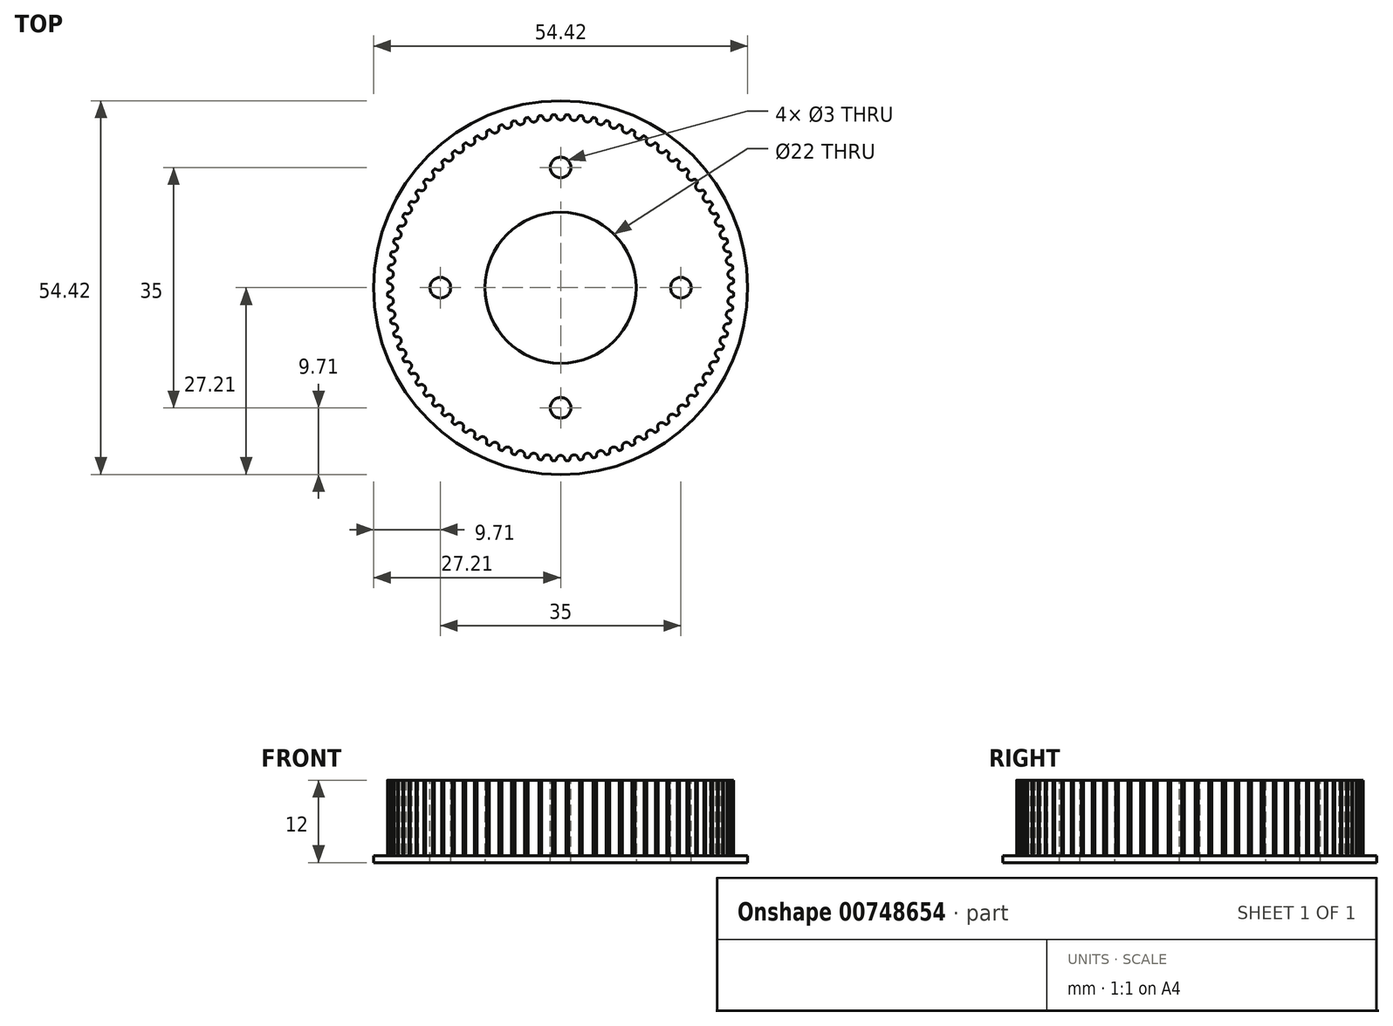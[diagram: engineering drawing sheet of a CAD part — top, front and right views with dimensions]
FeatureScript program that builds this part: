
annotation { "Feature Type Name" : "Feature", "Feature Type Description" : "" }
export const myFeature = defineFeature(function(context is Context, id is Id, definition is map)
    precondition{}
    {
        {
            assignVariable(context, id + "F0", {"name" : "Teeth", "anyValue" : 80});
        }
        {
            var Q0;
            Q0=qCreatedBy(makeId("Top.planeOp"),FACE);
            var sketch = newSketch(context, id + "F1", { "sketchPlane" : qUnion([Q0])});
            skCircle(sketch, "E0", {"center": v(0, 0) * mm, "radius": 25.21 * mm});
            skSolve(sketch);
        }
        {
            var Q0;
            Q0=qCreatedBy(makeId("Top.planeOp"),FACE);
            var sketch = newSketch(context, id + "F2", { "sketchPlane" : qUnion([Q0])});
            skArc(sketch, "E1.0", {"start": v(0.79, 25.2) * mm, "mid": v(0, 25.21) * mm, "end": v(-0.79, 25.2) * mm});
            skLineSegment(sketch, "E2", {"start": v(0, 0) * mm, "end": v(0, 25.03) * mm, "construction": true});
            skArc(sketch, "E3", {"start": v(0, 24.42) * mm, "mid": v(-0.38, 24.56) * mm, "end": v(-0.6, 24.9) * mm});
            skArc(sketch, "E4", {"start": v(-0.6, 24.9) * mm, "mid": v(-0.63, 25) * mm, "end": v(-0.68, 25.1) * mm});
            skArc(sketch, "E5", {"start": v(-0.68, 25.1) * mm, "mid": v(-0.72, 25.16) * mm, "end": v(-0.79, 25.2) * mm});
            skArc(sketch, "E6.MirrorCS", {"start": v(0, 24.42) * mm, "mid": v(0.38, 24.56) * mm, "end": v(0.6, 24.9) * mm});
            skArc(sketch, "E7.MirrorCS", {"start": v(0.68, 25.1) * mm, "mid": v(0.72, 25.16) * mm, "end": v(0.79, 25.2) * mm});
            skArc(sketch, "E8.MirrorCS", {"start": v(0.6, 24.9) * mm, "mid": v(0.63, 25) * mm, "end": v(0.68, 25.1) * mm});
            skSolve(sketch);
        }
        {
            var Q0;
            Q0=qSketchRegion(id+"F1",true);
            extrude(context, id + "F3", {"entities" : qUnion([Q0]), "depth" : 11 * mm, "offsetDistance" : 25 * mm});
        }
        {
            var Q0;
            Q0=makeQuery(id+"F2.imprint","IMPRINT",FACE,{"disambiguationData":[TD([[makeQuery(id+"F2.imprint","IMPRINT",EDGE,{"derivedFrom":sQuery(id+"F2.wireOp",EDGE,"E1.0")}),1.0]])]});
            extrude(context, id + "F4", {"entities" : qUnion([Q0]), "depth" : 25 * mm, "offsetDistance" : 25 * mm});
        }
        {
            var Q0;
            Q0=makeQuery(id+"F4.opExtrude","SWEPT_BODY",BODY,{"disambiguationData":[OSD([sQuery(id+"F2.wireOp",EDGE,"E1.0"),sQuery(id+"F2.wireOp",EDGE,"E3"),sQuery(id+"F2.wireOp",EDGE,"E4"),sQuery(id+"F2.wireOp",EDGE,"E5"),sQuery(id+"F2.wireOp",EDGE,"E6.MirrorCS"),sQuery(id+"F2.wireOp",EDGE,"E7.MirrorCS"),sQuery(id+"F2.wireOp",EDGE,"E8.MirrorCS")])]});
            var Q1;
            Q1=sQuery(id+"F1.wireOp",EDGE,"E0");
            circularPattern(context, id + "F5", {"operationType" : NewBodyOperationType.REMOVE, "entities" : qUnion([Q0]), "axis" : qUnion([Q1]), "angle" : 360 * degree, "instanceCount" : getVariable(context, 'Teeth'), "equalSpace" : true});
        }
        {
            var Q0;
            Q0=qCreatedBy(makeId("Top.planeOp"),FACE);
            var sketch = newSketch(context, id + "F6", { "sketchPlane" : qUnion([Q0])});
            skCircle(sketch, "E9", {"center": v(0, 0) * mm, "radius": 11 * mm});
            skSolve(sketch);
        }
        {
            var Q0;
            Q0=qSketchRegion(id+"F6",true);
            var Q1;
            Q1=sQuery(id+"F6.wireOp",EDGE,"E9");
            extrude(context, id + "F7", {"entities" : qUnion([Q0]), "operationType" : NewBodyOperationType.REMOVE, "surfaceEntities" : qUnion([Q1]), "endBound" : BoundingType.THROUGH_ALL, "depth" : 25 * mm, "offsetDistance" : 25 * mm});
        }
        {
            var Q0;
            Q0=qCreatedBy(makeId("Top.planeOp"),FACE);
            var sketch = newSketch(context, id + "F8", { "sketchPlane" : qUnion([Q0])});
            skCircle(sketch, "E10", {"center": v(0, 0) * mm, "radius": 26.21 * mm});
            skCircle(sketch, "E11.0", {"center": v(0, 0) * mm, "radius": 11 * mm});
            skCircle(sketch, "E12.0", {"center": v(0, 0) * mm, "radius": 27.21 * mm});
            skSolve(sketch);
        }
        {
            var Q0;
            Q0=makeQuery(id+"F3.opExtrude","CAP_FACE",FACE,{"disambiguationData":[OSD([sQuery(id+"F1.wireOp",EDGE,"E0")])],"isStart":false});
            var sketch = newSketch(context, id + "F9", { "sketchPlane" : qUnion([Q0])});
            skLineSegment(sketch, "E13", {"start": v(0, 0) * mm, "end": v(0, 17.5) * mm, "construction": true});
            skLineSegment(sketch, "E14", {"start": v(0, 0) * mm, "end": v(17.5, 0) * mm, "construction": true});
            skLineSegment(sketch, "E15", {"start": v(0, 0) * mm, "end": v(0, -17.5) * mm, "construction": true});
            skLineSegment(sketch, "E16", {"start": v(0, 0) * mm, "end": v(-17.5, 0) * mm, "construction": true});
            skCircle(sketch, "E17", {"center": v(0, 17.5) * mm, "radius": 1.5 * mm});
            skCircle(sketch, "E18", {"center": v(-17.5, 0) * mm, "radius": 1.5 * mm});
            skCircle(sketch, "E19", {"center": v(17.5, 0) * mm, "radius": 1.5 * mm});
            skCircle(sketch, "E20", {"center": v(0, -17.5) * mm, "radius": 1.5 * mm});
            skSolve(sketch);
        }
        {
            var Q0;
            Q0=makeQuery(id+"F8.imprint","IMPRINT",FACE,{"disambiguationData":[TD([[makeQuery(id+"F8.imprint","IMPRINT",EDGE,{"derivedFrom":sQuery(id+"F8.wireOp",EDGE,"E10")}),-1.0]])]});
            var Q1;
            Q1=makeQuery(id+"F8.imprint","IMPRINT",FACE,{"disambiguationData":[TD([[makeQuery(id+"F8.imprint","IMPRINT",EDGE,{"derivedFrom":sQuery(id+"F8.wireOp",EDGE,"E10")}),1.0]])]});
            var Q2;
            Q2=makeQuery(id+"F8.imprint","IMPRINT",FACE,{"disambiguationData":[TD([[makeQuery(id+"F8.imprint","IMPRINT",EDGE,{"derivedFrom":sQuery(id+"F8.wireOp",EDGE,"E11.0")}),1.0]])]});
            extrude(context, id + "F10", {"entities" : qUnion([Q0, Q1, Q2]), "operationType" : NewBodyOperationType.ADD, "oppositeDirection" : true, "depth" : 1 * mm, "offsetDistance" : 25 * mm});
        }
        {
            var Q0;
            Q0=makeQuery(id+"F6.imprint","IMPRINT",FACE,{"disambiguationData":[TD([[makeQuery(id+"F6.imprint","IMPRINT",EDGE,{"derivedFrom":sQuery(id+"F6.wireOp",EDGE,"E9")}),1.0]])]});
            extrude(context, id + "F11", {"entities" : qUnion([Q0]), "operationType" : NewBodyOperationType.REMOVE, "endBound" : BoundingType.THROUGH_ALL, "oppositeDirection" : true, "depth" : 25 * mm, "offsetDistance" : 25 * mm});
        }
        {
            var Q0;
            Q0 = qSketchRegion(id + "F9", true);
            extrude(context, id + "F12", {"entities" : qUnion([Q0]), "operationType" : NewBodyOperationType.REMOVE, "endBound" : BoundingType.THROUGH_ALL, "oppositeDirection" : true, "depth" : 25 * mm, "offsetDistance" : 25 * mm});
        }
    });
